# Revit family: Sanitary_Compound-Units_DURAVIT-AG_DE4938-D-Neo-Vanity-unit-wall-mounted
name_source: partatom
category: Furniture
revit_build: Autodesk Revit 2018 (Build: 20190510_1515(x64)
units: mm (PartAtom-declared; Revit-internal decimal feet)

## family parameters
Cut with Voids When Loaded = No
Host = Face
OmniClass Number = 23.19.31.17.11
OmniClass Title = Bathroom Units
Room Calculation Point = No
Shared = No

## types (13) — shared parameters
Always visible = Yes
BIMobject category = Compound Units
Date of publishing = 14.05.2021 00:00:00
Default Elevation = 1219 mm
Description = D-Neo Vanity unit wall-mounted White Matt 800x480x260 mm
Edition number = 1
IFC Classification = Furnishing Element
Manufacturer = Duravit
Manufacturer name = DURAVIT AG
Masterformat 2014 Code = 12 50 00
Masterformat 2014 Description = Furniture
Material main = Wood
Model = D-Neo Wall mounted console vanity unit 800x480x260 mm - DE4938
NBS Reference Code = 35-75-08
NBS Reference Description = Bathroom Cabinets
OmniClass Code = 23-19 31 17 11
OmniClass Description = Bathroom Units
Product Guid = 76dd9e51-e2c7-4199-bbc8-84292a9db5ec
Product SKU = d-neo-vanity-unit-wall-mounted-de4938
Product data url = https://bimobject.com
Product family = D-Neo
Product group = Vanity unit wall-mounted
Product name = D-Neo Wall mounted console vanity unit 800x480x260 mm - DE4938
QR code = https://bimobject.com
UNSPSC Code = 56
URL = https://duravit.com
Uniclass 1.4 Code = L8241
Uniclass 1.4 Description = Bathroom cabinets
Uniclass 2.0 Code = PR-35-75-08
Uniclass 2.0 Description = Bathroom Cabinets
Uniclass 2015 Code = Pr_40_30_78_05
Uniclass 2015 Name = Bathroom furniture
Uniformat II Code = E2010
Uniformat II Description = Fixed Furnishings
Weight Net (Kg) = 12

## per-type parameters (varying)
| type | Main material | Main material 90 |
| 07 - Concrete Grey Matt | Duravit - Wood - 07 - Concrete Grey Matt | Duravit - Wood - 07 - Concrete Grey Matt |
| 22 - White HG | Duravit - Wood - 22 - White HG | Duravit - Wood - 22 - White HG |
| 18 - White Matt | Duravit - Wood - 18 - White Matt | Duravit - Wood - 18 - White Matt |
| 91 - Taupe | Duravit - Wood - 91 - Taupe | Duravit - Wood - 91 - Taupe |
| 16 - Black Oak | Duravit - Wood - 16 - Black Oak | Duravit - Wood - 16 - Black Oak 90 |
| 21 - Walnut Dark | Duravit - Wood - 21 - Walnut Dark | Duravit - Wood - 21 - Walnut Dark 90 |
| 30 - Natural Oak | Duravit - Wood - 30 - Natural Oak | Duravit - Wood - 30 - Natural Oak 90 |
| 35 - Oak Terra | Duravit - Wood - 35 - Oak Terra | Duravit - Wood - 35 - Oak Terra 90 |
| 43 - Basalt Matt | Duravit - Wood - 43 - Basalt Matt | Duravit - Wood - 43 - Basalt Matt |
| 49 - Graphite Matt | Duravit - Wood - 49 - Graphite Matt | Duravit - Wood - 49 - Graphite Matt |
| 53 - Chestnut Dark | Duravit - Wood - 53 - Chestnut Dark | Duravit - Wood - 53 - Chestnut Dark 90 |
| 75 - Linen | Duravit - Wood - 75 - Linen | Duravit - Wood - 75 - Linen |
| 79 - Natural Walnut | Duravit - Wood - 79 - Natural Walnut | Duravit - Wood - 79 - Natural Walnut 90 |

## geometry (parser evidence)
native form markers: Sweep x4
no freeform markers — native parametric forms only
